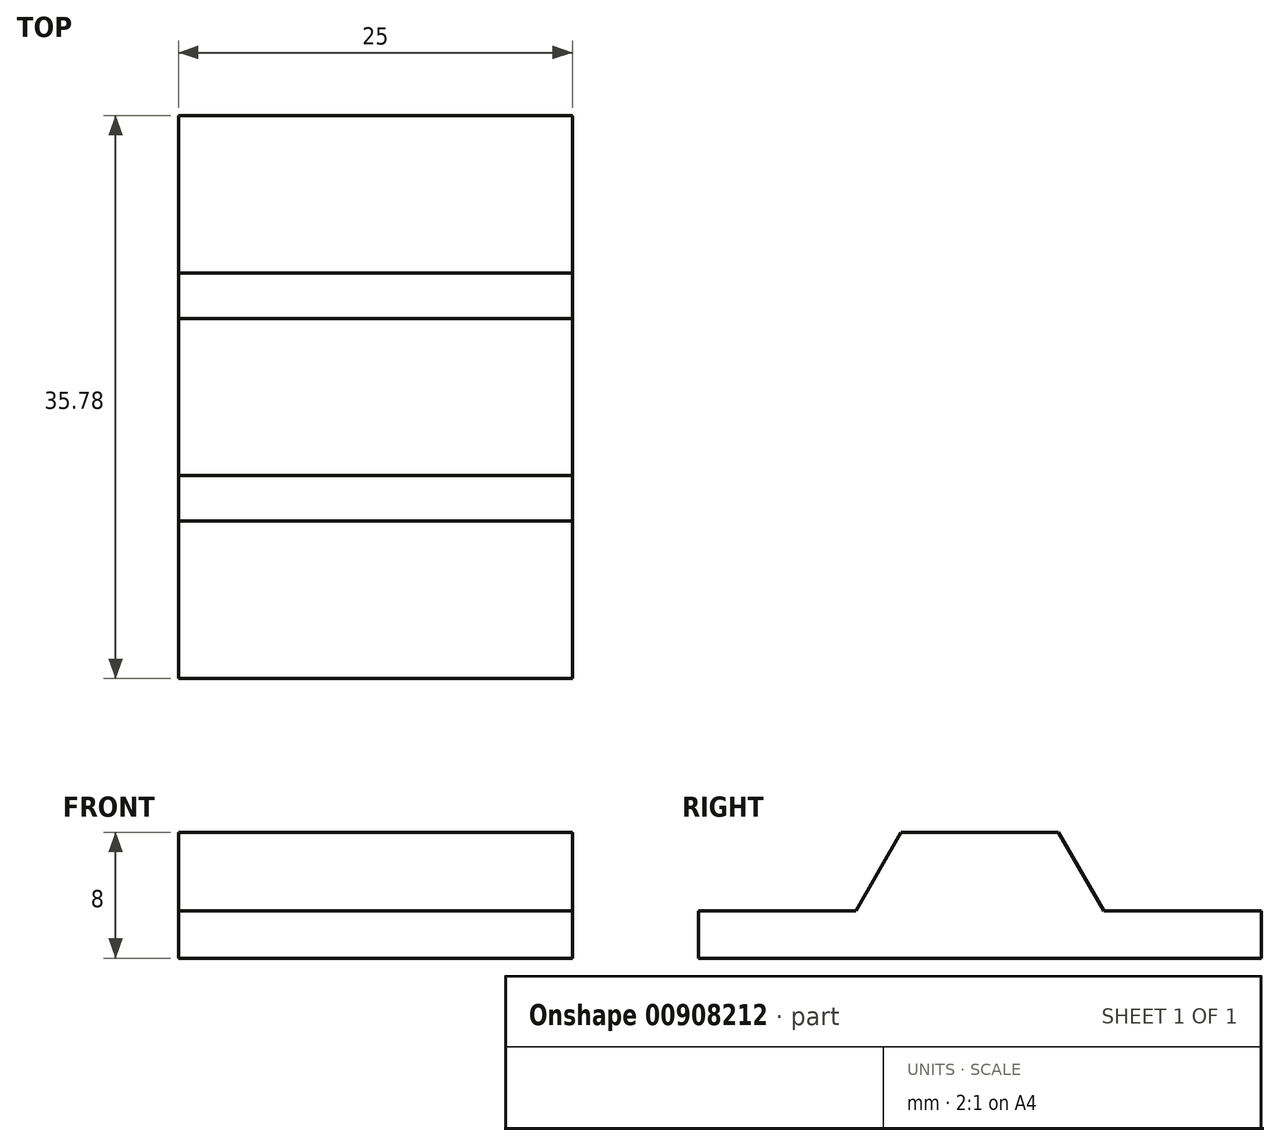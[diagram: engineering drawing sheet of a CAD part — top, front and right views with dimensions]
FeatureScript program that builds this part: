
annotation { "Feature Type Name" : "Feature", "Feature Type Description" : "" }
export const myFeature = defineFeature(function(context is Context, id is Id, definition is map)
    precondition{}
    {
        {
            var Q0;
            Q0=qCreatedBy(makeId("Right.planeOp"), FACE);
            var sketch = newSketch(context, id + "F0", { "sketchPlane" : qUnion([Q0])});
            skLineSegment(sketch, "E0", {"start": v(-17.89, 0) * mm, "end": v(-17.89, 3) * mm});
            skLineSegment(sketch, "E1", {"start": v(-17.89, 3) * mm, "end": v(-7.89, 3) * mm});
            skLineSegment(sketch, "E2", {"start": v(-7.89, 3) * mm, "end": v(-5, 8) * mm});
            skLineSegment(sketch, "E3", {"start": v(-5, 8) * mm, "end": v(0, 8) * mm});
            skLineSegment(sketch, "E4", {"start": v(-17.89, 0) * mm, "end": v(0, 0) * mm});
            skLineSegment(sketch, "E5.MirrorCS", {"start": v(7.89, 3) * mm, "end": v(5, 8) * mm});
            skLineSegment(sketch, "E6.MirrorCS", {"start": v(5, 8) * mm, "end": v(0, 8) * mm});
            skLineSegment(sketch, "E7.MirrorCS", {"start": v(17.89, 0) * mm, "end": v(17.89, 3) * mm});
            skLineSegment(sketch, "E8.MirrorCS", {"start": v(17.89, 3) * mm, "end": v(7.89, 3) * mm});
            skLineSegment(sketch, "E9.MirrorCS", {"start": v(17.89, 0) * mm, "end": v(0, 0) * mm});
            skSolve(sketch);
        }
        {
            var Q0;
            Q0 = qSketchRegion(id + "F0", true);
            extrude(context, id + "F1", {"entities" : qUnion([Q0]), "domain" : OperationDomain.MODEL, "flatOperationType" : FlatOperationType.REMOVE, "depth" : 25 * mm, "offsetDistance" : 25 * mm});
        }
    });
